# Revit family: Double_Sink-American_Standard-Quince-77DB3322_Series
name_source: partatom
category: Plumbing Fixtures
revit_build: Autodesk Revit 2014 (Build: 20130308_1515(x64)
units: mm (PartAtom-declared; Revit-internal decimal feet)

## types (2) — shared parameters
ADA Compliant = Yes
Assembly Code = D2010410
Basin Shape = Rectangular
Bowl Length = 16 1/8"
Bowl Width = 13 1/2"
CW Connection = Yes
CWFU = 3
Cold Water Connection Diameter = 1/2"
Cold Water Connection Radius = 1/4"
Cold Water Connection Width = 4"
Default Elevation = 34"
Description = Quince Double Bowl Kitchen Sink
Finish = Cast Iron-American Standard-308-Brilliant White
Gap = 29 9/16"
HW Connection = Yes
HWFU = 3
Height = 9"
Hot Water Connection Diameter = 1"
Hot Water Connection Radius = 1/4"
Hot Water Connection Width = 4"
Installation Type = Topmount
Length = 22 1/4"
Manufacturer = American Standard
Material = Cast Iron-American Standard-308-Brilliant White
Price = Prices may vary. Please consult Manufacturer Representative for most up-to-date price list.
Type Comments = 36" (914mm) cabinet required
URL = https://www.americanstandard-us.com
Vent Connection = No
WFU = 4
Warranty Information = Limited Lifetime Warranty
Waste Connection = Yes
Waste Connection Diameter = 1 1/2"
Waste Connection Offset = 11 1/8"
Waste Connection Radius = 3/4"
Waste Connection Width = 12 13/16"
Width = 32 7/8"

## per-type parameters (varying)
| type | 4 Hole Option | Hole Height |
| 77DB33223.308 | No | 1" |
| 77DB33224.308 | Yes | 2 53/64" |

note: column(s) folded — value = type name in every type: Model

## geometry (parser evidence)
native form markers: Sweep x1
no freeform markers — native parametric forms only
